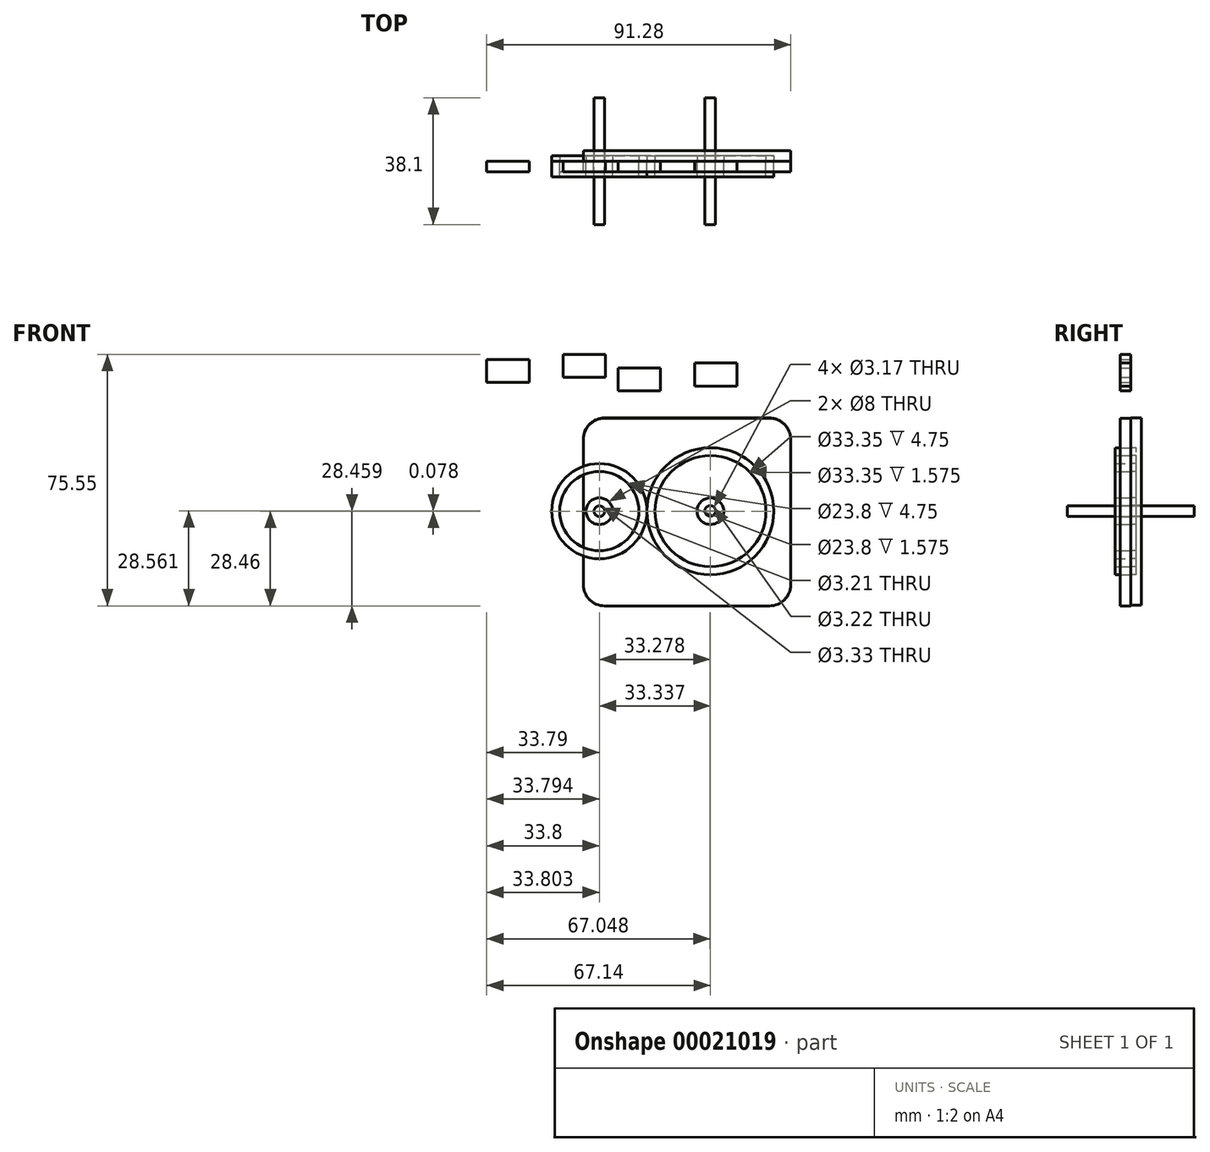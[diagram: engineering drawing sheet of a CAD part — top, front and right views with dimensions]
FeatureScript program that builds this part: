
annotation { "Feature Type Name" : "Feature", "Feature Type Description" : "" }
export const myFeature = defineFeature(function(context is Context, id is Id, definition is map)
    precondition{}
    {
        {
            var Q0;
            Q0=qCreatedBy(makeId("Front.planeOp"),FACE);
            var sketch = newSketch(context, id + "F0", { "sketchPlane" : qUnion([Q0])});
            skCircle(sketch, "E0", {"center": v(0, 0) * mm, "radius": 19.05 * mm});
            skCircle(sketch, "E1", {"center": v(-0.06, 0.08) * mm, "radius": 1.59 * mm});
            skCircle(sketch, "E2", {"center": v(0, 0) * mm, "radius": 4 * mm});
            skCircle(sketch, "E3", {"center": v(0, 0) * mm, "radius": 16.68 * mm});
            skSolve(sketch);
        }
        {
            var Q0;
            Q0=qCreatedBy(makeId("Front.planeOp"),FACE);
            var sketch = newSketch(context, id + "F1", { "sketchPlane" : qUnion([Q0])});
            skCircle(sketch, "E4", {"center": v(-33.34, 0) * mm, "radius": 14.29 * mm});
            skCircle(sketch, "E5", {"center": v(-33.34, 0) * mm, "radius": 1.59 * mm});
            skCircle(sketch, "E6", {"center": v(-33.34, 0) * mm, "radius": 4 * mm});
            skCircle(sketch, "E7", {"center": v(-33.34, 0) * mm, "radius": 11.9 * mm});
            skSolve(sketch);
        }
        {
            var Q0;
            Q0=qCreatedBy(makeId("Front.planeOp"),FACE);
            var sketch = newSketch(context, id + "F2", { "sketchPlane" : qUnion([Q0])});
            skCircle(sketch, "E8", {"center": v(0, 0) * mm, "radius": 1.59 * mm});
            skCircle(sketch, "E9", {"center": v(-33.34, 0) * mm, "radius": 1.59 * mm});
            skSolve(sketch);
        }
        {
            var Q0;
            Q0=makeQuery(id+"F0.imprint","IMPRINT",FACE,{"disambiguationData":[TD([[makeQuery(id+"F0.imprint","IMPRINT",EDGE,{"derivedFrom":sQuery(id+"F0.wireOp",EDGE,"E1")}),-1.0]])]});
            var Q1;
            Q1=makeQuery(id+"F0.imprint","IMPRINT",FACE,{"disambiguationData":[TD([[makeQuery(id+"F0.imprint","IMPRINT",EDGE,{"derivedFrom":sQuery(id+"F0.wireOp",EDGE,"E0")}),1.0]])]});
            var Q2;
            Q2=makeQuery(id+"F1.imprint","IMPRINT",FACE,{"disambiguationData":[TD([[makeQuery(id+"F1.imprint","IMPRINT",EDGE,{"derivedFrom":sQuery(id+"F1.wireOp",EDGE,"E5")}),-1.0]])]});
            var Q3;
            Q3=makeQuery(id+"F1.imprint","IMPRINT",FACE,{"disambiguationData":[TD([[makeQuery(id+"F1.imprint","IMPRINT",EDGE,{"derivedFrom":sQuery(id+"F1.wireOp",EDGE,"E4")}),1.0]])]});
            extrude(context, id + "F3", {"entities" : qUnion([Q0, Q1, Q2, Q3]), "oppositeDirection" : true, "depth" : 1.57 * mm});
        }
        {
            var Q0;
            Q0=makeQuery(id+"F0.imprint","IMPRINT",FACE,{"disambiguationData":[TD([[makeQuery(id+"F0.imprint","IMPRINT",EDGE,{"derivedFrom":sQuery(id+"F0.wireOp",EDGE,"E1")}),-1.0]])]});
            var Q1;
            Q1=makeQuery(id+"F0.imprint","IMPRINT",FACE,{"disambiguationData":[TD([[makeQuery(id+"F0.imprint","IMPRINT",EDGE,{"derivedFrom":sQuery(id+"F0.wireOp",EDGE,"E0")}),1.0]])]});
            var Q2;
            Q2=makeQuery(id+"F1.imprint","IMPRINT",FACE,{"disambiguationData":[TD([[makeQuery(id+"F1.imprint","IMPRINT",EDGE,{"derivedFrom":sQuery(id+"F1.wireOp",EDGE,"E5")}),-1.0]])]});
            var Q3;
            Q3=makeQuery(id+"F1.imprint","IMPRINT",FACE,{"disambiguationData":[TD([[makeQuery(id+"F1.imprint","IMPRINT",EDGE,{"derivedFrom":sQuery(id+"F1.wireOp",EDGE,"E4")}),1.0]])]});
            extrude(context, id + "F4", {"entities" : qUnion([Q0, Q1, Q2, Q3]), "depth" : 4.75 * mm});
        }
        {
            var Q0;
            Q0=makeQuery(id+"F1.imprint","IMPRINT",FACE,{"disambiguationData":[TD([[makeQuery(id+"F1.imprint","IMPRINT",EDGE,{"derivedFrom":sQuery(id+"F1.wireOp",EDGE,"E6")}),-1.0]])]});
            var Q1;
            Q1=makeQuery(id+"F0.imprint","IMPRINT",FACE,{"disambiguationData":[TD([[makeQuery(id+"F0.imprint","IMPRINT",EDGE,{"derivedFrom":sQuery(id+"F0.wireOp",EDGE,"E2")}),-1.0]])]});
            extrude(context, id + "F5", {"entities" : qUnion([Q0, Q1]), "depth" : 3.17 * mm});
        }
        {
            var Q0;
            Q0=makeQuery(id+"F2.imprint","IMPRINT",FACE,{"disambiguationData":[TD([[makeQuery(id+"F2.imprint","IMPRINT",EDGE,{"derivedFrom":sQuery(id+"F2.wireOp",EDGE,"E9")}),1.0]])]});
            var Q1;
            Q1=makeQuery(id+"F0.imprint","IMPRINT",FACE,{"disambiguationData":[TD([[makeQuery(id+"F0.imprint","IMPRINT",EDGE,{"derivedFrom":sQuery(id+"F0.wireOp",EDGE,"E1")}),1.0]])]});
            extrude(context, id + "F6", {"entities" : qUnion([Q0, Q1]), "endBound" : BoundingType.SYMMETRIC, "depth" : 38.1 * mm});
        }
        {
            var Q0;
            Q0=qCreatedBy(makeId("Front.planeOp"),FACE);
            var sketch = newSketch(context, id + "F7", { "sketchPlane" : qUnion([Q0])});
            skLineSegment(sketch, "E10.bottom", {"start": v(17.79, 27.86) * mm, "end": v(-31.8, 27.86) * mm});
            skLineSegment(sketch, "E10.top", {"start": v(17.79, -28.46) * mm, "end": v(-31.8, -28.46) * mm});
            skLineSegment(sketch, "E10.left", {"start": v(24.14, 21.51) * mm, "end": v(24.14, -22.1) * mm});
            skLineSegment(sketch, "E10.right", {"start": v(-38.14, 21.51) * mm, "end": v(-38.14, -22.1) * mm});
            skCircle(sketch, "E11", {"center": v(-33.35, 0) * mm, "radius": 1.67 * mm});
            skPoint(sketch, "E12.first.point", {"position": v(0, 1.68) * mm});
            skPoint(sketch, "E12.second.point", {"position": v(-0.21, -1.51) * mm});
            skPoint(sketch, "E12.third.point", {"position": v(1.1, -0.98) * mm});
            skPoint(sketch, "E13.visualSharp", {"position": v(24.14, 27.86) * mm});
            skArc(sketch, "E13.filletArc", {"start": v(24.14, 21.51) * mm, "mid": v(22.28, 26) * mm, "end": v(17.79, 27.86) * mm});
            skPoint(sketch, "E14.visualSharp", {"position": v(-38.14, 27.86) * mm});
            skArc(sketch, "E14.filletArc", {"start": v(-31.8, 27.86) * mm, "mid": v(-36.28, 26) * mm, "end": v(-38.14, 21.51) * mm});
            skPoint(sketch, "E15.visualSharp", {"position": v(-38.14, -28.46) * mm});
            skArc(sketch, "E15.filletArc", {"start": v(-38.14, -22.1) * mm, "mid": v(-36.28, -26.6) * mm, "end": v(-31.8, -28.46) * mm});
            skPoint(sketch, "E16.visualSharp", {"position": v(24.14, -28.46) * mm});
            skArc(sketch, "E16.filletArc", {"start": v(17.79, -28.46) * mm, "mid": v(22.28, -26.6) * mm, "end": v(24.14, -22.1) * mm});
            skCircle(sketch, "E17", {"center": v(-0.1, 0.09) * mm, "radius": 1.6 * mm});
            skSolve(sketch);
        }
        {
            var Q0;
            Q0=qCreatedBy(makeId("Front.planeOp"),FACE);
            var sketch = newSketch(context, id + "F8", { "sketchPlane" : qUnion([Q0])});
            skLineSegment(sketch, "E18.bottom", {"start": v(-31.78, 28) * mm, "end": v(17.72, 28) * mm});
            skLineSegment(sketch, "E18.top", {"start": v(-31.78, -28.19) * mm, "end": v(17.72, -28.19) * mm});
            skLineSegment(sketch, "E18.left", {"start": v(-38.13, 21.66) * mm, "end": v(-38.13, -21.84) * mm});
            skLineSegment(sketch, "E18.right", {"start": v(24.07, 21.66) * mm, "end": v(24.07, -21.84) * mm});
            skCircle(sketch, "E19", {"center": v(-33.35, 0) * mm, "radius": 1.6 * mm});
            skCircle(sketch, "E20", {"center": v(-0.1, 0.1) * mm, "radius": 1.61 * mm});
            skPoint(sketch, "E20.first.point", {"position": v(0, 1.7) * mm});
            skPoint(sketch, "E20.second.point", {"position": v(-0.21, -1.5) * mm});
            skPoint(sketch, "E20.third.point", {"position": v(1.1, -0.98) * mm});
            skPoint(sketch, "E21.visualSharp", {"position": v(24.07, 28) * mm});
            skArc(sketch, "E21.filletArc", {"start": v(24.07, 21.66) * mm, "mid": v(22.2, 26.15) * mm, "end": v(17.72, 28) * mm});
            skPoint(sketch, "E22.visualSharp", {"position": v(-38.13, 28) * mm});
            skArc(sketch, "E22.filletArc", {"start": v(-31.78, 28) * mm, "mid": v(-36.27, 26.15) * mm, "end": v(-38.13, 21.66) * mm});
            skPoint(sketch, "E23.visualSharp", {"position": v(-38.13, -28.19) * mm});
            skArc(sketch, "E23.filletArc", {"start": v(-38.13, -21.84) * mm, "mid": v(-36.27, -26.33) * mm, "end": v(-31.78, -28.19) * mm});
            skPoint(sketch, "E24.visualSharp", {"position": v(24.07, -28.19) * mm});
            skArc(sketch, "E24.filletArc", {"start": v(17.72, -28.19) * mm, "mid": v(22.2, -26.33) * mm, "end": v(24.07, -21.84) * mm});
            skSolve(sketch);
        }
        {
            var Q0;
            Q0 = qSketchRegion(id + "F7", true);
            extrude(context, id + "F9", {"entities" : qUnion([Q0]), "depth" : 3.17 * mm});
        }
        {
            var Q0;
            Q0 = qSketchRegion(id + "F8", true);
            extrude(context, id + "F10", {"entities" : qUnion([Q0]), "oppositeDirection" : true, "depth" : 3.17 * mm});
        }
        {
            var Q0;
            Q0=qCreatedBy(makeId("Front.planeOp"),FACE);
            var sketch = newSketch(context, id + "F11", { "sketchPlane" : qUnion([Q0])});
            skLineSegment(sketch, "E25.bottom", {"start": v(-67.14, 45.6) * mm, "end": v(-54.44, 45.6) * mm});
            skLineSegment(sketch, "E25.top", {"start": v(-67.14, 38.73) * mm, "end": v(-54.44, 38.73) * mm});
            skLineSegment(sketch, "E25.left", {"start": v(-67.14, 45.6) * mm, "end": v(-67.14, 38.73) * mm});
            skLineSegment(sketch, "E25.right", {"start": v(-54.44, 45.6) * mm, "end": v(-54.44, 38.73) * mm});
            skLineSegment(sketch, "E26.bottom", {"start": v(-44.2, 47.1) * mm, "end": v(-31.5, 47.1) * mm});
            skLineSegment(sketch, "E26.top", {"start": v(-44.2, 40.22) * mm, "end": v(-31.5, 40.22) * mm});
            skLineSegment(sketch, "E26.left", {"start": v(-44.2, 47.1) * mm, "end": v(-44.2, 40.22) * mm});
            skLineSegment(sketch, "E26.right", {"start": v(-31.5, 47.1) * mm, "end": v(-31.5, 40.22) * mm});
            skLineSegment(sketch, "E27.bottom", {"start": v(-27.66, 42.98) * mm, "end": v(-14.96, 42.98) * mm});
            skLineSegment(sketch, "E27.top", {"start": v(-27.66, 36.1) * mm, "end": v(-14.96, 36.1) * mm});
            skLineSegment(sketch, "E27.left", {"start": v(-27.66, 42.98) * mm, "end": v(-27.66, 36.1) * mm});
            skLineSegment(sketch, "E27.right", {"start": v(-14.96, 42.98) * mm, "end": v(-14.96, 36.1) * mm});
            skLineSegment(sketch, "E28.bottom", {"start": v(-4.72, 44.47) * mm, "end": v(7.98, 44.47) * mm});
            skLineSegment(sketch, "E28.top", {"start": v(-4.72, 37.6) * mm, "end": v(7.98, 37.6) * mm});
            skLineSegment(sketch, "E28.left", {"start": v(-4.72, 44.47) * mm, "end": v(-4.72, 37.6) * mm});
            skLineSegment(sketch, "E28.right", {"start": v(7.98, 44.47) * mm, "end": v(7.98, 37.6) * mm});
            skSolve(sketch);
        }
        {
            var Q0;
            Q0=makeQuery(id+"F11.imprint","IMPRINT",FACE,{"disambiguationData":[TD([[makeQuery(id+"F11.imprint","IMPRINT",EDGE,{"derivedFrom":sQuery(id+"F11.wireOp",EDGE,"E25.bottom")}),-1.0]])]});
            var Q1;
            Q1=makeQuery(id+"F11.imprint","IMPRINT",FACE,{"disambiguationData":[TD([[makeQuery(id+"F11.imprint","IMPRINT",EDGE,{"derivedFrom":sQuery(id+"F11.wireOp",EDGE,"E26.bottom")}),-1.0]])]});
            var Q2;
            Q2=makeQuery(id+"F11.imprint","IMPRINT",FACE,{"disambiguationData":[TD([[makeQuery(id+"F11.imprint","IMPRINT",EDGE,{"derivedFrom":sQuery(id+"F11.wireOp",EDGE,"E27.bottom")}),-1.0]])]});
            var Q3;
            Q3=makeQuery(id+"F11.imprint","IMPRINT",FACE,{"disambiguationData":[TD([[makeQuery(id+"F11.imprint","IMPRINT",EDGE,{"derivedFrom":sQuery(id+"F11.wireOp",EDGE,"E28.bottom")}),-1.0]])]});
            extrude(context, id + "F12", {"entities" : qUnion([Q0, Q1, Q2, Q3]), "depth" : 3.17 * mm});
        }
    });
